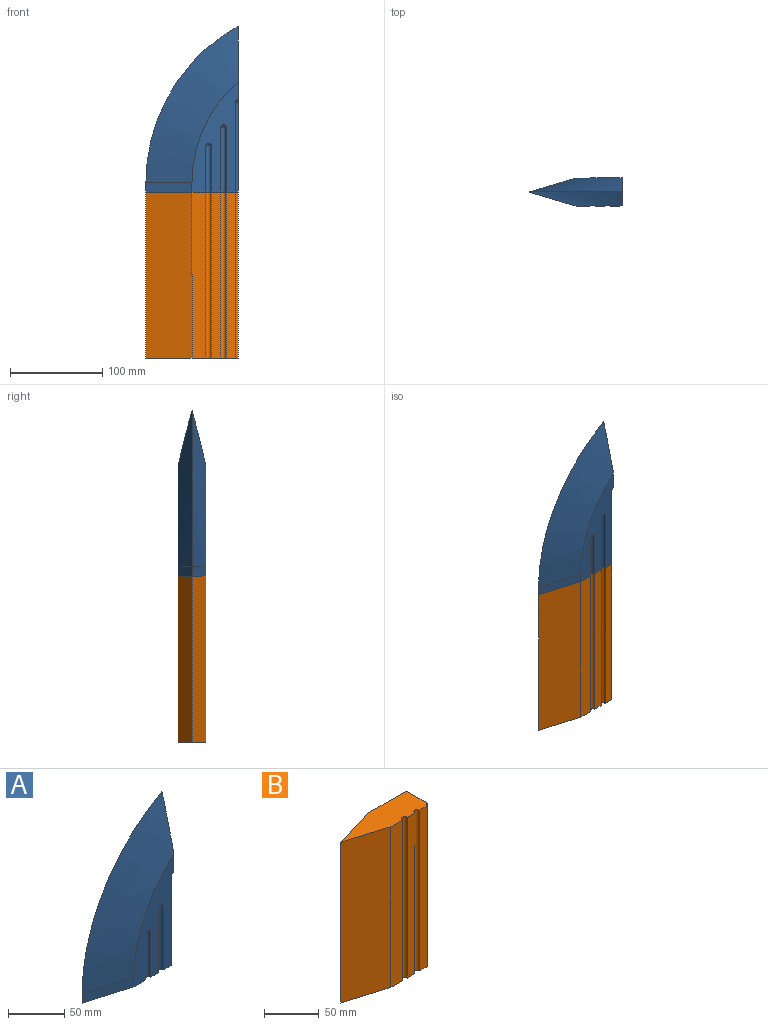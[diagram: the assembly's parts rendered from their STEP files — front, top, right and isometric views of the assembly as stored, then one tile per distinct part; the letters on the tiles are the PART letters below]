
ASSEMBLY  parts=2 mates=1
PART A: 14 faces, bbox 124.3x30x180 mm
  f0: plane 180x30mm, normal (1,0,0), area 4213mm2, adj f1,f2,f3,f4,f6,f12,f13
  f1: plane 100x30mm, normal (0,0,-1), area 2214.7mm2, adj f0,f2,f3,f5,f7,f8,f10,f13
  f2: plane 119.32x50mm, normal (0,-1,0), area 3245.7mm2, adj f0,f1,f4,f5,f8,f9,f10,f11
  f3: plane 119.32x50mm, normal (0,1,0), area 4292.1mm2, adj f0,f1,f6,f7
  f4: cone r=144.5mm half-angle=73.3deg, axis (0,1,0), area 8655.7mm2, adj f0,f2,f5,f6
  f5: plane 50x15mm, normal (-0.29,-0.96,0), area 522mm2, adj f1,f2,f4,f7
  f6: cone r=194.5mm half-angle=73.3deg, axis (0,-1,0), area 8655.7mm2, adj f0,f3,f4,f7
  f7: plane 50x15mm, normal (-0.29,0.96,0), area 522mm2, adj f1,f3,f5,f6
  f8: cylinder r=3mm len=50mm, axis (0,0,1), area 471.2mm2, adj f1,f2,f9
  f9: sphere r=3mm, area 28.3mm2, adj f2,f8
  f10: cylinder r=3mm len=70mm, axis (0,0,-1), area 659.7mm2, adj f1,f2,f11
  f11: sphere r=3mm, area 28.3mm2, adj f2,f10
  f12: sphere r=3mm, area 14.1mm2, adj f0,f2,f13
  f13: cylinder r=3mm len=97mm, axis (0,0,-1), area 457.1mm2, adj f0,f1,f2,f12
PART B: 12 faces, bbox 100x30x180 mm
  f0: plane 180x27mm, normal (1,0,0), area 4860mm2, adj f3,f4,f6,f11
  f1: plane 180x10mm, normal (0,-1,0), area 1800mm2, adj f3,f4,f10,f11
  f2: plane 180x10mm, normal (0,-1,0), area 1800mm2, adj f3,f4,f9,f10
  f3: plane 100x30mm, normal (0,0,-1), area 2214.7mm2, adj f0,f1,f2,f5,f6,f7,f8,f9
  f4: plane 100x30mm, normal (0,0,1), area 2214.7mm2, adj f0,f1,f2,f5,f6,f7,f8,f9
  f5: plane 180x15mm, normal (0,-1,0), area 2700mm2, adj f3,f4,f8,f9
  f6: plane 180x50mm, normal (0,1,0), area 9000mm2, adj f0,f3,f4,f7
  f7: plane 180x50mm, normal (-0.29,0.96,0), area 9396.3mm2, adj f3,f4,f6,f8
  f8: plane 180x50mm, normal (-0.29,-0.96,0), area 9396.3mm2, adj f3,f4,f5,f7
  f9: cylinder r=3mm len=180mm, axis (0,0,-1), area 1696.5mm2, adj f2,f3,f4,f5
  f10: cylinder r=3mm len=180mm, axis (0,0,1), area 1696.5mm2, adj f1,f2,f3,f4
  f11: cylinder r=3mm len=180mm, axis (0,0,-1), area 848.2mm2, adj f0,f1,f3,f4
PLACE A t=(-49.32,28.06,-30.76)mm
PLACE B t=(-49.32,28.06,-125.76)mm
MATE fastened B.f4 <-> A.f1  axis (0,0,1) through (-38.52,13.28,-35.76)mm
